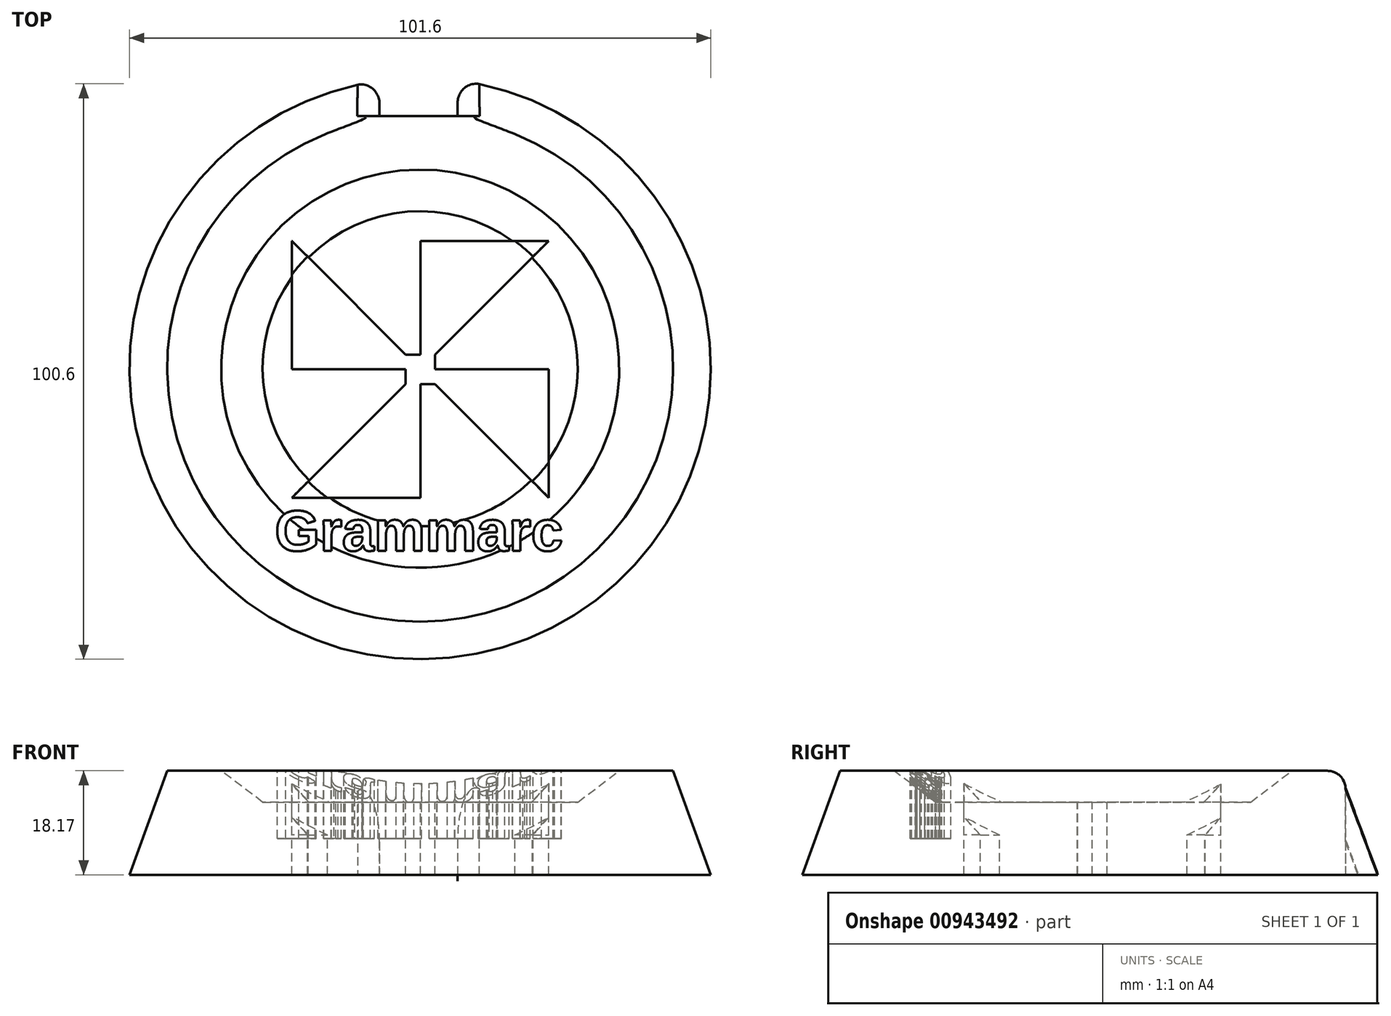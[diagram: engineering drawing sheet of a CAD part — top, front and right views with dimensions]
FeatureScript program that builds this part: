
annotation { "Feature Type Name" : "Feature", "Feature Type Description" : "" }
export const myFeature = defineFeature(function(context is Context, id is Id, definition is map)
    precondition{}
    {
        {
            var Q0;
            Q0=qCreatedBy(makeId("Front.planeOp"),FACE);
            var sketch = newSketch(context, id + "F0", { "sketchPlane" : qUnion([Q0])});
            skLineSegment(sketch, "E0", {"start": v(0, 0) * mm, "end": v(-40.62, 0) * mm});
            skLineSegment(sketch, "E1", {"start": v(-40.62, 0) * mm, "end": v(-50.8, 0) * mm});
            skLineSegment(sketch, "E2", {"start": v(-50.8, 0) * mm, "end": v(-44.22, 18.17) * mm});
            skLineSegment(sketch, "E3", {"start": v(-44.22, 18.17) * mm, "end": v(-34.79, 18.17) * mm});
            skLineSegment(sketch, "E4", {"start": v(-34.79, 18.17) * mm, "end": v(-27.54, 12.7) * mm});
            skLineSegment(sketch, "E5", {"start": v(-27.54, 12.7) * mm, "end": v(0, 12.7) * mm});
            skLineSegment(sketch, "E6", {"start": v(0, 12.7) * mm, "end": v(0, 0) * mm});
            skSolve(sketch);
        }
        {
            var Q0;
            Q0=qCreatedBy(makeId("Top.planeOp"),FACE);
            cPlane(context, id + "F1", {"entities" : qUnion([Q0]), "cplaneType" : CPlaneType.OFFSET, "offset" : 25.4 * mm, "width" : 152.4 * mm, "height" : 152.4 * mm});
        }
        {
            var Q0;
            Q0 = qSketchRegion(id + "F0", true);
            var Q1;
            Q1=makeQuery(id+"F0.imprint","IMPRINT",FACE,{"disambiguationData":[TD([[makeQuery(id+"F0.imprint","IMPRINT",EDGE,{"derivedFrom":sQuery(id+"F0.wireOp",EDGE,"E0")}),-1.0]])]});
            var Q2;
            Q2 = qSketchRegion(id + "F3", true);
            var Q3;
            Q3=sQuery(id+"F0.wireOp",EDGE,"E6");
            revolve(context, id + "F2", {"surfaceOperationType" : NewSurfaceOperationType.NEW, "entities" : qUnion([Q0, Q1, Q2]), "axis" : qUnion([Q3]), "revolveType" : RevolveType.FULL});
        }
        {
            var Q0;
            Q0=qCreatedBy(id+"F1.planeOp",FACE);
            var sketch = newSketch(context, id + "F3", { "sketchPlane" : qUnion([Q0])});
            skLineSegment(sketch, "E7", {"start": v(0.03, -22.57) * mm, "end": v(0.03, 22.33) * mm});
            skLineSegment(sketch, "E8", {"start": v(-22.42, -0.12) * mm, "end": v(22.48, -0.12) * mm});
            skLineSegment(sketch, "E9", {"start": v(-22.42, 22.33) * mm, "end": v(22.48, -22.57) * mm});
            skLineSegment(sketch, "E10", {"start": v(22.48, 22.33) * mm, "end": v(-22.42, -22.57) * mm});
            skLineSegment(sketch, "E11", {"start": v(0.03, 22.33) * mm, "end": v(22.48, 22.33) * mm});
            skLineSegment(sketch, "E12", {"start": v(22.48, -0.12) * mm, "end": v(22.48, -22.57) * mm});
            skLineSegment(sketch, "E13", {"start": v(-22.42, -0.12) * mm, "end": v(-22.42, 22.33) * mm});
            skLineSegment(sketch, "E14", {"start": v(0.03, -22.57) * mm, "end": v(-22.42, -22.57) * mm});
            skLineSegment(sketch, "E15.bottom", {"start": v(-2.54, 2.45) * mm, "end": v(2.61, 2.45) * mm});
            skLineSegment(sketch, "E15.top", {"start": v(-2.54, -2.7) * mm, "end": v(2.61, -2.7) * mm});
            skLineSegment(sketch, "E15.left", {"start": v(-2.54, 2.45) * mm, "end": v(-2.54, -2.7) * mm});
            skLineSegment(sketch, "E15.right", {"start": v(2.61, 2.45) * mm, "end": v(2.61, -2.7) * mm});
            skSolve(sketch);
        }
        {
            var Q0;
            Q0 = qSketchRegion(id + "F3", true);
            extrude(context, id + "F4", {"entities" : qUnion([Q0]), "operationType" : NewBodyOperationType.REMOVE, "oppositeDirection" : true, "depth" : 25.4 * mm, "offsetDistance" : 25.4 * mm});
        }
        {
            var Q0;
            Q0=qCreatedBy(makeId("Front.planeOp"),FACE);
            var sketch = newSketch(context, id + "F5", { "sketchPlane" : qUnion([Q0])});
            skLineSegment(sketch, "E16", {"start": v(-45.23, 14.36) * mm, "end": v(-50.72, 0) * mm});
            skLineSegment(sketch, "E17", {"start": v(-50.72, 0) * mm, "end": v(-39.24, 0) * mm});
            skLineSegment(sketch, "E18", {"start": v(-39.24, 0) * mm, "end": v(-27.79, 0) * mm});
            skLineSegment(sketch, "E19", {"start": v(-27.79, 0) * mm, "end": v(-27.79, 6.97) * mm});
            skLineSegment(sketch, "E20", {"start": v(-45.23, 14.36) * mm, "end": v(-37.18, 14.36) * mm});
            skLineSegment(sketch, "E21", {"start": v(-37.18, 14.36) * mm, "end": v(-27.79, 6.97) * mm});
            skSolve(sketch);
        }
        {
            var Q0;
            Q0 = qSketchRegion(id + "F5", true);
            var Q1;
            Q1=sQuery(id+"F0.wireOp",EDGE,"E6");
            revolve(context, id + "F6", {"operationType" : NewBodyOperationType.ADD, "surfaceOperationType" : NewSurfaceOperationType.NEW, "entities" : qUnion([Q0]), "axis" : qUnion([Q1]), "revolveType" : RevolveType.FULL});
        }
        {
            var Q0;
            Q0=qCreatedBy(makeId("Top.planeOp"),FACE);
            var sketch = newSketch(context, id + "F7", { "sketchPlane" : qUnion([Q0])});
            skLineSegment(sketch, "E22.bottom", {"start": v(-7.1, 65.96) * mm, "end": v(6.54, 65.96) * mm});
            skLineSegment(sketch, "E22.top", {"start": v(-7.1, 44.16) * mm, "end": v(6.54, 44.16) * mm});
            skLineSegment(sketch, "E22.left", {"start": v(-7.1, 65.96) * mm, "end": v(-7.1, 44.16) * mm});
            skLineSegment(sketch, "E22.right", {"start": v(6.54, 65.96) * mm, "end": v(6.54, 44.16) * mm});
            skSolve(sketch);
        }
        {
            var Q0;
            Q0 = qSketchRegion(id + "F7", true);
            extrude(context, id + "F8", {"entities" : qUnion([Q0]), "operationType" : NewBodyOperationType.REMOVE, "depth" : 25.4 * mm, "offsetDistance" : 25.4 * mm});
        }
        {
            var Q0;
            Q0=makeQuery(id+"F8.boolean.opBoolean","INTERSECT",EDGE,{"derivedFrom":[makeQuery(id+"F2.opRevolve","SWEPT_FACE",FACE,{"disambiguationData":[OSD([sQuery(id+"F0.wireOp",EDGE,"E2")])]}),makeQuery(id+"F8.opExtrude","SWEPT_FACE",FACE,{"disambiguationData":[OSD([sQuery(id+"F7.wireOp",EDGE,"E22.left")])]})]});
            fillet(context, id + "F9", {"entities" : qUnion([Q0]), "radius" : 3.17 * mm, "tangentPropagation" : true, "allowEdgeOverflow" : false});
        }
        {
            var Q0;
            Q0=makeQuery(id+"F8.boolean.opBoolean","INTERSECT",EDGE,{"derivedFrom":[makeQuery(id+"F2.opRevolve","SWEPT_FACE",FACE,{"disambiguationData":[OSD([sQuery(id+"F0.wireOp",EDGE,"E2")])]}),makeQuery(id+"F8.opExtrude","SWEPT_FACE",FACE,{"disambiguationData":[OSD([sQuery(id+"F7.wireOp",EDGE,"E22.right")])]})]});
            fillet(context, id + "F10", {"entities" : qUnion([Q0]), "radius" : 3.17 * mm, "tangentPropagation" : true, "allowEdgeOverflow" : false});
        }
        {
            var Q0;
            Q0=makeQuery(id+"F8.boolean.opBoolean","INTERSECT",EDGE,{"derivedFrom":[makeQuery(id+"F2.opRevolve","SWEPT_FACE",FACE,{"disambiguationData":[OSD([sQuery(id+"F0.wireOp",EDGE,"E3")])]}),makeQuery(id+"F8.opExtrude","SWEPT_FACE",FACE,{"disambiguationData":[OSD([sQuery(id+"F7.wireOp",EDGE,"E22.top")])]})]});
            fillet(context, id + "F11", {"entities" : qUnion([Q0]), "radius" : 3.17 * mm, "tangentPropagation" : true, "allowEdgeOverflow" : false});
        }
        {
            var Q0;
            Q0=qCreatedBy(id+"F1.planeOp",FACE);
            var sketch = newSketch(context, id + "F12", { "sketchPlane" : qUnion([Q0])});
            skText(sketch, "E23", { "text": "Grammarc", "fontName": "Arimo-Bold.ttf"});
            const initialGuessF12  = {"E23": [-0.0254, -0.03184, 1, 0, 0.00725]};
            skSetInitialGuess(sketch, initialGuessF12);
            skSolve(sketch);
        }
        {
            var Q0;
            Q0 = qSketchRegion(id + "F12", true);
            extrude(context, id + "F13", {"entities" : qUnion([Q0]), "operationType" : NewBodyOperationType.REMOVE, "oppositeDirection" : true, "depth" : 19.05 * mm, "offsetDistance" : 25.4 * mm});
        }
    });
